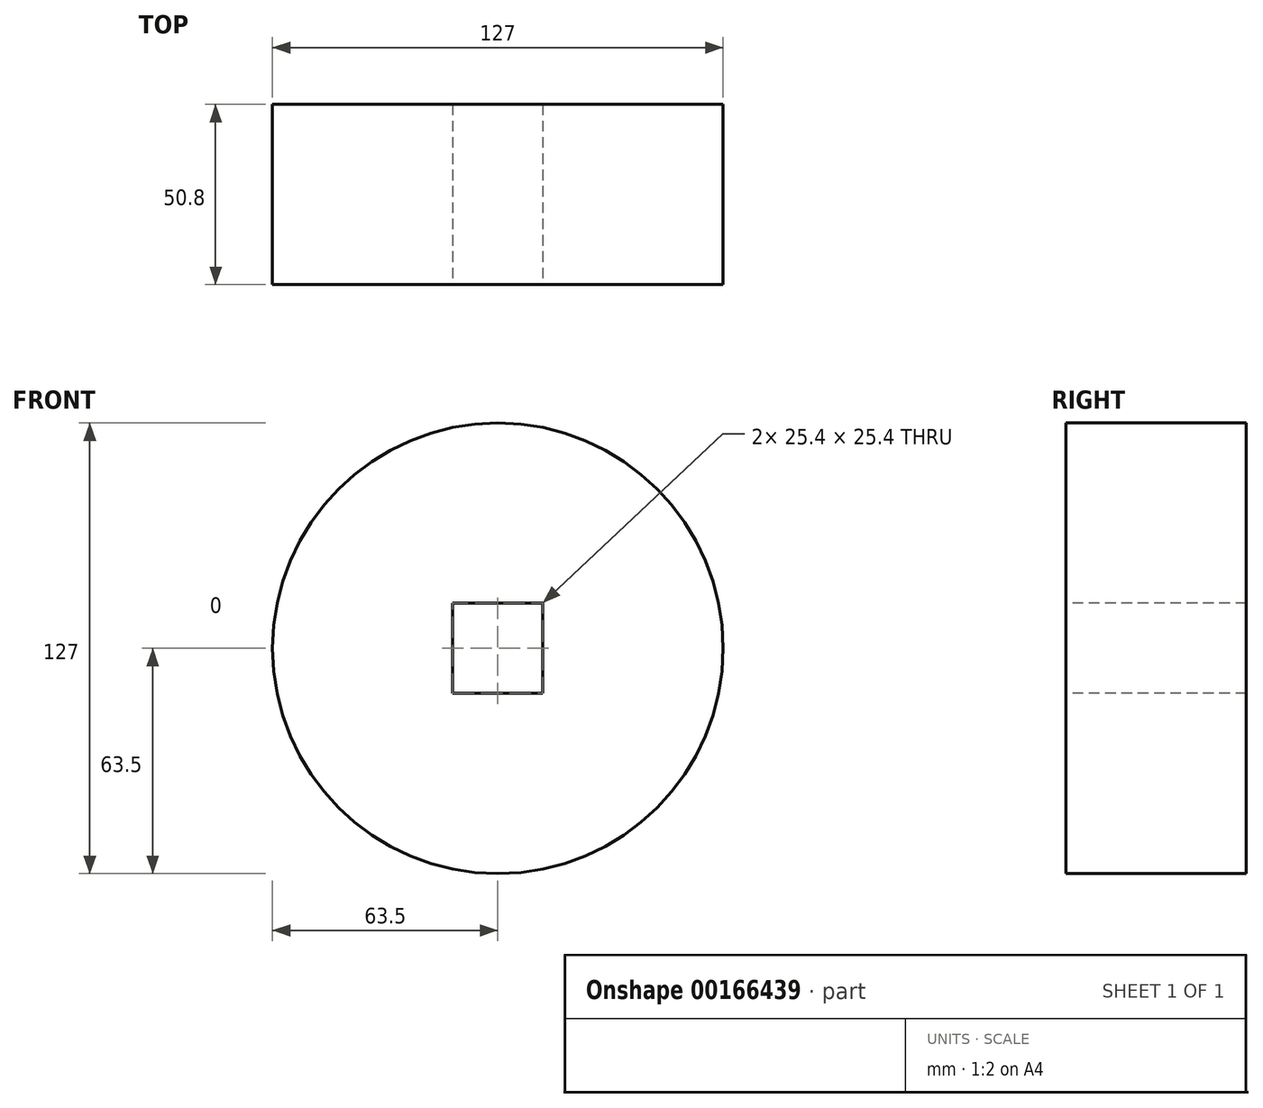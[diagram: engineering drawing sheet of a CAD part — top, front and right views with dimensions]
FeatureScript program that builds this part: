
annotation { "Feature Type Name" : "Feature", "Feature Type Description" : "" }
export const myFeature = defineFeature(function(context is Context, id is Id, definition is map)
    precondition{}
    {
        {
            var Q0;
            Q0=qCreatedBy(makeId("Front.planeOp"),FACE);
            var sketch = newSketch(context, id + "F0", { "sketchPlane" : qUnion([Q0])});
            skCircle(sketch, "E0", {"center": v(0, 0) * mm, "radius": 63.5 * mm});
            skSolve(sketch);
        }
        {
            var Q0;
            Q0 = qSketchRegion(id + "F0", true);
            extrude(context, id + "F1", {"entities" : qUnion([Q0]), "depth" : 50.8 * mm});
        }
        {
            var Q0;
            Q0=makeQuery(id+"F1.opExtrude","CAP_FACE",FACE,{"disambiguationData":[OSD([sQuery(id+"F0.wireOp",EDGE,"E0")])],"isStart":false});
            var sketch = newSketch(context, id + "F2", { "sketchPlane" : qUnion([Q0])});
            skLineSegment(sketch, "E1.bottom", {"start": v(-12.7, 12.7) * mm, "end": v(12.7, 12.7) * mm});
            skLineSegment(sketch, "E1.top", {"start": v(-12.7, -12.7) * mm, "end": v(12.7, -12.7) * mm});
            skLineSegment(sketch, "E1.left", {"start": v(-12.7, 12.7) * mm, "end": v(-12.7, -12.7) * mm});
            skLineSegment(sketch, "E1.right", {"start": v(12.7, 12.7) * mm, "end": v(12.7, -12.7) * mm});
            skPoint(sketch, "E1.middle", {"position": v(0, 0) * mm});
            skSolve(sketch);
        }
        {
            var Q0;
            Q0 = qSketchRegion(id + "F2", true);
            extrude(context, id + "F3", {"entities" : qUnion([Q0]), "operationType" : NewBodyOperationType.REMOVE, "endBound" : BoundingType.THROUGH_ALL, "oppositeDirection" : true, "depth" : 25 * mm});
        }
    });
